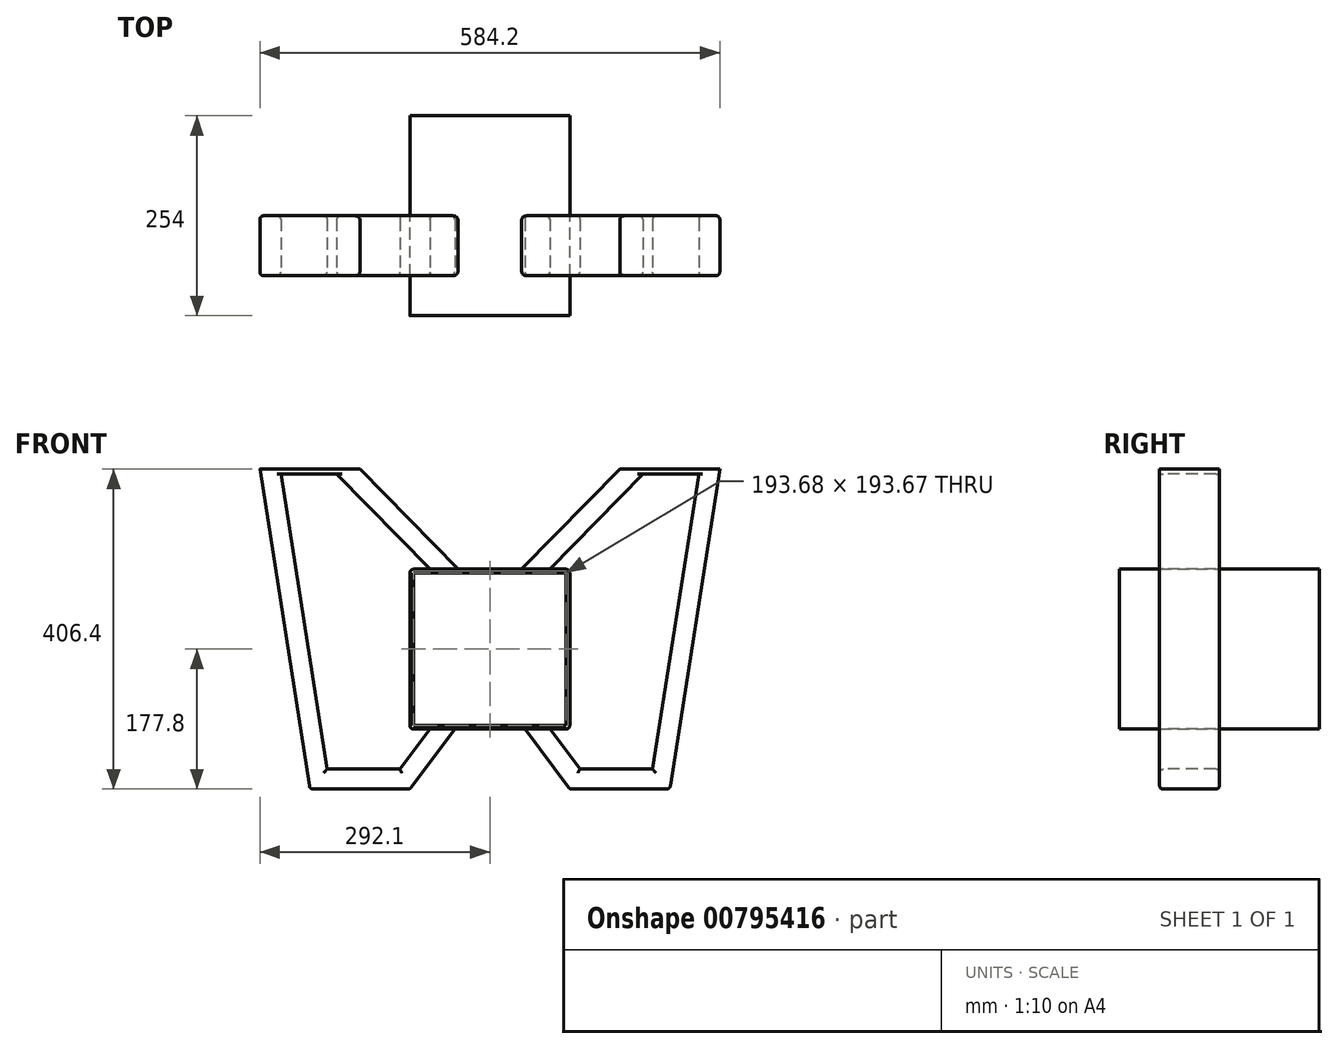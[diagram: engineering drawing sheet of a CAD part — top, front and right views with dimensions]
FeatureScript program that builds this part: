
annotation { "Feature Type Name" : "Feature", "Feature Type Description" : "" }
export const myFeature = defineFeature(function(context is Context, id is Id, definition is map)
    precondition{}
    {
        {
            var Q0;
            Q0=qCreatedBy(makeId("Front.planeOp"),FACE);
            var sketch = newSketch(context, id + "F0", { "sketchPlane" : qUnion([Q0])});
            skLineSegment(sketch, "E0", {"start": v(-228.6, 0) * mm, "end": v(-101.6, 0) * mm});
            skLineSegment(sketch, "E1", {"start": v(-101.6, 0) * mm, "end": v(-44.45, 76.2) * mm});
            skLineSegment(sketch, "E2", {"start": v(44.45, 76.2) * mm, "end": v(101.6, 0) * mm});
            skLineSegment(sketch, "E3", {"start": v(101.6, 0) * mm, "end": v(228.6, 0) * mm});
            skLineSegment(sketch, "E4", {"start": v(228.6, 0) * mm, "end": v(292.1, 406.4) * mm});
            skLineSegment(sketch, "E5", {"start": v(292.1, 406.4) * mm, "end": v(165.1, 406.4) * mm});
            skLineSegment(sketch, "E6", {"start": v(165.1, 406.4) * mm, "end": v(40.64, 279.4) * mm});
            skLineSegment(sketch, "E7", {"start": v(-40.64, 279.4) * mm, "end": v(-165.1, 406.4) * mm});
            skLineSegment(sketch, "E8", {"start": v(-165.1, 406.4) * mm, "end": v(-292.1, 406.4) * mm});
            skLineSegment(sketch, "E9", {"start": v(-292.1, 406.4) * mm, "end": v(-228.6, 0) * mm});
            skLineSegment(sketch, "E10", {"start": v(0, 366.73) * mm, "end": v(0, -83.74) * mm, "construction": true});
            skLineSegment(sketch, "E11.0", {"start": v(-76.2, 279.4) * mm, "end": v(-200.66, 406.4) * mm});
            skLineSegment(sketch, "E11.1", {"start": v(-266.4, 406.4) * mm, "end": v(-206.86, 25.4) * mm});
            skLineSegment(sketch, "E11.2", {"start": v(-206.86, 25.4) * mm, "end": v(-114.3, 25.4) * mm});
            skLineSegment(sketch, "E11.3", {"start": v(-114.3, 25.4) * mm, "end": v(-76.2, 76.2) * mm});
            skLineSegment(sketch, "E12.0", {"start": v(206.86, 25.4) * mm, "end": v(266.4, 406.4) * mm});
            skLineSegment(sketch, "E12.1", {"start": v(200.66, 406.4) * mm, "end": v(76.2, 279.4) * mm});
            skLineSegment(sketch, "E12.3", {"start": v(76.2, 76.2) * mm, "end": v(114.3, 25.4) * mm});
            skLineSegment(sketch, "E12.4", {"start": v(114.3, 25.4) * mm, "end": v(206.86, 25.4) * mm});
            skLineSegment(sketch, "E13.0", {"start": v(-194.44, 400.05) * mm, "end": v(-265.4, 400.05) * mm});
            skLineSegment(sketch, "E14.0", {"start": v(265.4, 400.05) * mm, "end": v(194.44, 400.05) * mm});
            skLineSegment(sketch, "E15", {"start": v(-101.6, 279.4) * mm, "end": v(101.6, 279.4) * mm});
            skLineSegment(sketch, "E16", {"start": v(101.6, 279.4) * mm, "end": v(101.6, 76.2) * mm});
            skLineSegment(sketch, "E17", {"start": v(101.6, 76.2) * mm, "end": v(-101.6, 76.2) * mm});
            skLineSegment(sketch, "E18", {"start": v(-101.6, 76.2) * mm, "end": v(-101.6, 279.4) * mm});
            skLineSegment(sketch, "E19.0", {"start": v(-96.84, 274.64) * mm, "end": v(96.84, 274.64) * mm});
            skLineSegment(sketch, "E19.1", {"start": v(-96.84, 80.96) * mm, "end": v(-96.84, 274.64) * mm});
            skLineSegment(sketch, "E19.2", {"start": v(96.84, 80.96) * mm, "end": v(-96.84, 80.96) * mm});
            skLineSegment(sketch, "E19.3", {"start": v(96.84, 274.64) * mm, "end": v(96.84, 80.96) * mm});
            skSolve(sketch);
        }
        {
            var Q0;
            {var subQ4=sQuery(id+"F0.wireOp",EDGE,"E7");Q0=makeQuery(id+"F0.imprint","IMPRINT",FACE,{"disambiguationData":[TD([[makeQuery(id+"F0.imprint","IMPRINT",EDGE,{"derivedFrom":subQ4}),1.0]])]});}
            var Q1;
            {var subQ5=sQuery(id+"F0.wireOp",EDGE,"E13.0");Q1=makeQuery(id+"F0.imprint","IMPRINT",FACE,{"disambiguationData":[TD([[makeQuery(id+"F0.imprint","IMPRINT",EDGE,{"derivedFrom":subQ5}),-1.0]])]});}
            var Q2;
            Q2=makeQuery(id+"F0.imprint","IMPRINT",FACE,{"disambiguationData":[TD([[makeQuery(id+"F0.imprint","IMPRINT",EDGE,{"derivedFrom":sQuery(id+"F0.wireOp",EDGE,"E0")}),1.0]])]});
            var Q3;
            {var subQ6=sQuery(id+"F0.wireOp",EDGE,"E6");Q3=makeQuery(id+"F0.imprint","IMPRINT",FACE,{"disambiguationData":[TD([[makeQuery(id+"F0.imprint","IMPRINT",EDGE,{"derivedFrom":subQ6}),1.0]])]});}
            var Q4;
            {var subQ5=sQuery(id+"F0.wireOp",EDGE,"E2");Q4=makeQuery(id+"F0.imprint","IMPRINT",FACE,{"disambiguationData":[TD([[makeQuery(id+"F0.imprint","IMPRINT",EDGE,{"derivedFrom":subQ5}),1.0]])]});}
            var Q5;
            {var subQ5=sQuery(id+"F0.wireOp",EDGE,"E14.0");Q5=makeQuery(id+"F0.imprint","IMPRINT",FACE,{"disambiguationData":[TD([[makeQuery(id+"F0.imprint","IMPRINT",EDGE,{"derivedFrom":subQ5}),-1.0]])]});}
            extrude(context, id + "F1", {"entities" : qUnion([Q0, Q1, Q2, Q3, Q4, Q5]), "oppositeDirection" : true, "depth" : 76.2 * mm, "offsetDistance" : 25.4 * mm});
        }
        {
            var Q0;
            {var subQ4=sQuery(id+"F0.wireOp",EDGE,"E16");Q0=makeQuery(id+"F0.imprint","IMPRINT",FACE,{"disambiguationData":[TD([[makeQuery(id+"F0.imprint","IMPRINT",EDGE,{"derivedFrom":subQ4}),-1.0]])]});}
            extrude(context, id + "F2", {"entities" : qUnion([Q0]), "depth" : 50.8 * mm, "offsetDistance" : 25.4 * mm, "hasSecondDirection" : true, "secondDirectionOppositeDirection" : true, "secondDirectionDepth" : 203.2 * mm});
        }
        {
            var Q0;
            Q0=makeQuery(id+"F2.opExtrude","SWEPT_EDGE",EDGE,{"disambiguationData":[OSD([sQuery(id+"F0.wireOp",EDGE,"E15"),sQuery(id+"F0.wireOp",EDGE,"E18")])]});
            var Q1;
            Q1=makeQuery(id+"F2.opExtrude","SWEPT_EDGE",EDGE,{"disambiguationData":[OSD([sQuery(id+"F0.wireOp",EDGE,"E15"),sQuery(id+"F0.wireOp",EDGE,"E16")])]});
            var Q2;
            Q2=makeQuery(id+"F2.opExtrude","SWEPT_EDGE",EDGE,{"disambiguationData":[OSD([sQuery(id+"F0.wireOp",EDGE,"E16"),sQuery(id+"F0.wireOp",EDGE,"E17")])]});
            var Q3;
            Q3=makeQuery(id+"F2.opExtrude","SWEPT_EDGE",EDGE,{"disambiguationData":[OSD([sQuery(id+"F0.wireOp",EDGE,"E17"),sQuery(id+"F0.wireOp",EDGE,"E18")])]});
            fillet(context, id + "F3", {"entities" : qUnion([Q0, Q1, Q2, Q3]), "tangentPropagation" : true, "radius" : 5.08 * mm, "defaultsChanged" : false, "vertexSettings" : [], "allowEdgeOverflow" : false});
        }
        {
            var Q0;
            Q0=makeQuery(id+"F1.opExtrude","CAP_EDGE",EDGE,{"disambiguationData":[OSD([sQuery(id+"F0.wireOp",EDGE,"E7")])],"isStart":false});
            var Q1;
            Q1=makeQuery(id+"F1.opExtrude","CAP_EDGE",EDGE,{"disambiguationData":[OSD([sQuery(id+"F0.wireOp",EDGE,"E7")])],"isStart":true});
            var Q2;
            Q2=makeQuery(id+"F1.opExtrude","CAP_EDGE",EDGE,{"disambiguationData":[OSD([sQuery(id+"F0.wireOp",EDGE,"E11.0")])],"isStart":true});
            var Q3;
            Q3=makeQuery(id+"F1.opExtrude","CAP_EDGE",EDGE,{"disambiguationData":[OSD([sQuery(id+"F0.wireOp",EDGE,"E11.1")])],"isStart":true});
            var Q4;
            Q4=makeQuery(id+"F1.opExtrude","CAP_EDGE",EDGE,{"disambiguationData":[OSD([sQuery(id+"F0.wireOp",EDGE,"E9")])],"isStart":true});
            var Q5;
            Q5=makeQuery(id+"F1.opExtrude","CAP_EDGE",EDGE,{"disambiguationData":[OSD([sQuery(id+"F0.wireOp",EDGE,"E11.1")])],"isStart":false});
            var Q6;
            Q6=makeQuery(id+"F1.opExtrude","CAP_EDGE",EDGE,{"disambiguationData":[OSD([sQuery(id+"F0.wireOp",EDGE,"E11.2")])],"isStart":true});
            var Q7;
            Q7=makeQuery(id+"F1.opExtrude","CAP_EDGE",EDGE,{"disambiguationData":[OSD([sQuery(id+"F0.wireOp",EDGE,"E0")])],"isStart":true});
            var Q8;
            Q8=makeQuery(id+"F1.opExtrude","CAP_EDGE",EDGE,{"disambiguationData":[OSD([sQuery(id+"F0.wireOp",EDGE,"E6")])],"isStart":true});
            var Q9;
            Q9=makeQuery(id+"F1.opExtrude","CAP_EDGE",EDGE,{"disambiguationData":[OSD([sQuery(id+"F0.wireOp",EDGE,"E6")])],"isStart":false});
            var Q10;
            Q10=makeQuery(id+"F1.opExtrude","CAP_EDGE",EDGE,{"disambiguationData":[OSD([sQuery(id+"F0.wireOp",EDGE,"E12.1")])],"isStart":true});
            var Q11;
            Q11=makeQuery(id+"F1.opExtrude","CAP_EDGE",EDGE,{"disambiguationData":[OSD([sQuery(id+"F0.wireOp",EDGE,"E12.0")])],"isStart":true});
            var Q12;
            Q12=makeQuery(id+"F1.opExtrude","CAP_EDGE",EDGE,{"disambiguationData":[OSD([sQuery(id+"F0.wireOp",EDGE,"E4")])],"isStart":true});
            var Q13;
            Q13=makeQuery(id+"F1.opExtrude","CAP_EDGE",EDGE,{"disambiguationData":[OSD([sQuery(id+"F0.wireOp",EDGE,"E4")])],"isStart":false});
            var Q14;
            Q14=makeQuery(id+"F1.opExtrude","CAP_EDGE",EDGE,{"disambiguationData":[OSD([sQuery(id+"F0.wireOp",EDGE,"E12.3")])],"isStart":true});
            var Q15;
            Q15=makeQuery(id+"F1.opExtrude","CAP_EDGE",EDGE,{"disambiguationData":[OSD([sQuery(id+"F0.wireOp",EDGE,"E2")])],"isStart":true});
            var Q16;
            Q16=makeQuery(id+"F1.opExtrude","CAP_EDGE",EDGE,{"disambiguationData":[OSD([sQuery(id+"F0.wireOp",EDGE,"E12.3")])],"isStart":false});
            var Q17;
            Q17=makeQuery(id+"F1.opExtrude","CAP_EDGE",EDGE,{"disambiguationData":[OSD([sQuery(id+"F0.wireOp",EDGE,"E12.4")])],"isStart":false});
            var Q18;
            Q18=makeQuery(id+"F1.opExtrude","CAP_EDGE",EDGE,{"disambiguationData":[OSD([sQuery(id+"F0.wireOp",EDGE,"E12.4")])],"isStart":true});
            var Q19;
            Q19=makeQuery(id+"F1.opExtrude","CAP_EDGE",EDGE,{"disambiguationData":[OSD([sQuery(id+"F0.wireOp",EDGE,"E3")])],"isStart":true});
            var Q20;
            Q20=makeQuery(id+"F1.opExtrude","SWEPT_EDGE",EDGE,{"disambiguationData":[OSD([sQuery(id+"F0.wireOp",EDGE,"E3"),sQuery(id+"F0.wireOp",EDGE,"E4")])]});
            var Q21;
            Q21=makeQuery(id+"F1.opExtrude","SWEPT_EDGE",EDGE,{"disambiguationData":[OSD([sQuery(id+"F0.wireOp",EDGE,"E0"),sQuery(id+"F0.wireOp",EDGE,"E9")])]});
            var Q22;
            Q22=makeQuery(id+"F1.opExtrude","CAP_EDGE",EDGE,{"disambiguationData":[OSD([sQuery(id+"F0.wireOp",EDGE,"E9")])],"isStart":false});
            var Q23;
            Q23=makeQuery(id+"F1.opExtrude","CAP_EDGE",EDGE,{"disambiguationData":[OSD([sQuery(id+"F0.wireOp",EDGE,"E0")])],"isStart":false});
            var Q24;
            Q24=makeQuery(id+"F1.opExtrude","CAP_EDGE",EDGE,{"disambiguationData":[OSD([sQuery(id+"F0.wireOp",EDGE,"E11.2")])],"isStart":false});
            var Q25;
            Q25=makeQuery(id+"F1.opExtrude","CAP_EDGE",EDGE,{"disambiguationData":[OSD([sQuery(id+"F0.wireOp",EDGE,"E11.3")])],"isStart":true});
            var Q26;
            Q26=makeQuery(id+"F1.opExtrude","CAP_EDGE",EDGE,{"disambiguationData":[OSD([sQuery(id+"F0.wireOp",EDGE,"E11.3")])],"isStart":false});
            var Q27;
            Q27=makeQuery(id+"F1.opExtrude","CAP_EDGE",EDGE,{"disambiguationData":[OSD([sQuery(id+"F0.wireOp",EDGE,"E1")])],"isStart":false});
            var Q28;
            Q28=makeQuery(id+"F1.opExtrude","CAP_EDGE",EDGE,{"disambiguationData":[OSD([sQuery(id+"F0.wireOp",EDGE,"E3")])],"isStart":false});
            var Q29;
            Q29=makeQuery(id+"F1.opExtrude","CAP_EDGE",EDGE,{"disambiguationData":[OSD([sQuery(id+"F0.wireOp",EDGE,"E12.0")])],"isStart":false});
            var Q30;
            Q30=makeQuery(id+"F1.opExtrude","CAP_EDGE",EDGE,{"disambiguationData":[OSD([sQuery(id+"F0.wireOp",EDGE,"E12.1")])],"isStart":false});
            var Q31;
            Q31=makeQuery(id+"F1.opExtrude","CAP_EDGE",EDGE,{"disambiguationData":[OSD([sQuery(id+"F0.wireOp",EDGE,"E11.0")])],"isStart":false});
            var Q32;
            Q32=makeQuery(id+"F1.opExtrude","CAP_EDGE",EDGE,{"disambiguationData":[OSD([sQuery(id+"F0.wireOp",EDGE,"E2")])],"isStart":false});
            var Q33;
            Q33=makeQuery(id+"F1.opExtrude","SWEPT_EDGE",EDGE,{"disambiguationData":[OSD([sQuery(id+"F0.wireOp",EDGE,"E2"),sQuery(id+"F0.wireOp",EDGE,"E3")])]});
            var Q34;
            Q34=makeQuery(id+"F1.opExtrude","CAP_EDGE",EDGE,{"disambiguationData":[OSD([sQuery(id+"F0.wireOp",EDGE,"E1")])],"isStart":true});
            var Q35;
            Q35=makeQuery(id+"F1.opExtrude","SWEPT_EDGE",EDGE,{"disambiguationData":[OSD([sQuery(id+"F0.wireOp",EDGE,"E0"),sQuery(id+"F0.wireOp",EDGE,"E1")])]});
            fillet(context, id + "F4", {"entities" : qUnion([Q0, Q1, Q2, Q3, Q4, Q5, Q6, Q7, Q8, Q9, Q10, Q11, Q12, Q13, Q14, Q15, Q16, Q17, Q18, Q19, Q20, Q21, Q22, Q23, Q24, Q25, Q26, Q27, Q28, Q29, Q30, Q31, Q32, Q33, Q34, Q35]), "tangentPropagation" : true, "radius" : 4.76 * mm, "defaultsChanged" : true, "vertexSettings" : [], "allowEdgeOverflow" : false});
        }
    });
